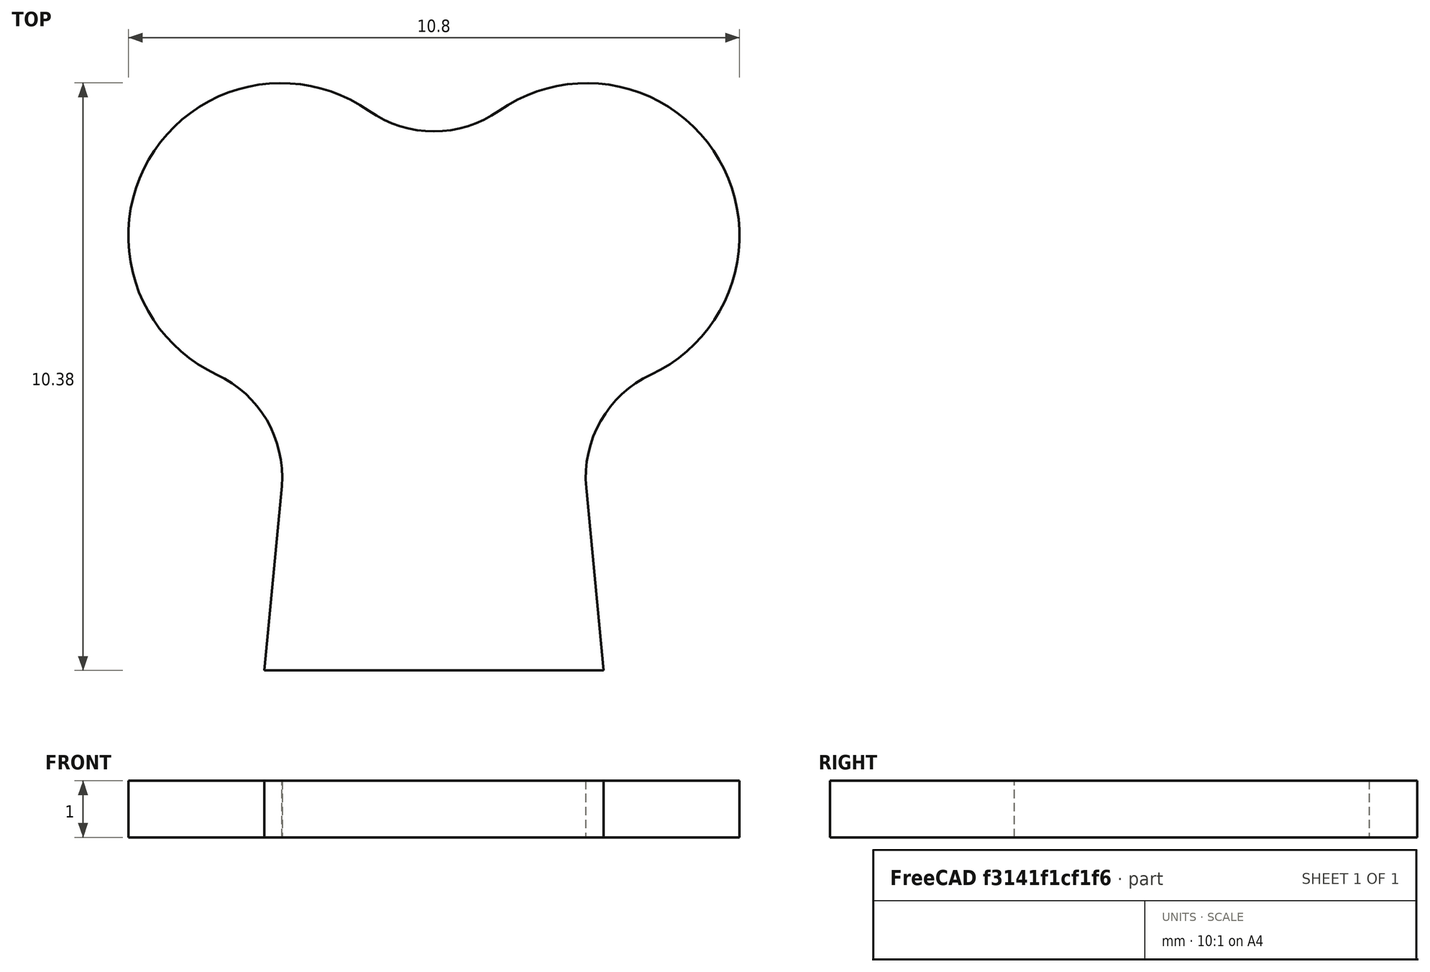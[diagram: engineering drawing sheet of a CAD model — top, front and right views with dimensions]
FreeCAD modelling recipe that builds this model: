
FCSTD DOCUMENT  (FreeCAD 0.18.1R)
Label: PCB_Telemetre_Diametral
License: All rights reserved
LicenseURL: http://en.wikipedia.org/wiki/All_rights_reserved
objects: Sketcher::SketchObject×1, PartDesign::Pad×1, PartDesign::Body×1
note: 4 computed .brp shape members not serialized (recipe doc carries the construction recipe); baked Part::Feature solids carry a one-line shape summary decoded from their .brp

FEATURE [Sketcher::SketchObject] Sketch
  MapMode = 5
  Support = -> [XY_Plane]
  sketch-geometry (11):
    g0: LineSegment StartX=3 StartY=0 StartZ=0 EndX=-3 EndY=0 EndZ=0
    g1: Circle [constr] CenterX=-2.7 CenterY=7.67654 CenterZ=0 NormalX=0 NormalY=0 NormalZ=1 AngleXU=0 Radius=2.7
    g2: Circle [constr] CenterX=2.7 CenterY=7.67654 CenterZ=0 NormalX=0 NormalY=0 NormalZ=1 AngleXU=0 Radius=2.7
    g3: Circle [constr] CenterX=0 CenterY=3 CenterZ=0 NormalX=0 NormalY=0 NormalZ=1 AngleXU=0 Radius=2.7
    g4: ArcOfCircle CenterX=0 CenterY=11.5236 CenterZ=0 NormalX=0 NormalY=0 NormalZ=1 AngleXU=0 Radius=2 StartAngle=4.10043 EndAngle=5.32434
    g5: ArcOfCircle CenterX=-2.7 CenterY=7.67654 CenterZ=0 NormalX=0 NormalY=0 NormalZ=1 AngleXU=0 Radius=2.7 StartAngle=0.958846 EndAngle=4.27718
    g6: ArcOfCircle CenterX=-4.68151 CenterY=3.41466 CenterZ=0 NormalX=0 NormalY=0 NormalZ=1 AngleXU=0 Radius=2 StartAngle=6.20461 EndAngle=7.41878
    g7: LineSegment StartX=-3 StartY=0 StartZ=0 EndX=-2.68768 EndY=3.25767 EndZ=0
    g8: ArcOfCircle CenterX=2.7 CenterY=7.67654 CenterZ=0 NormalX=0 NormalY=0 NormalZ=1 AngleXU=0 Radius=2.7 StartAngle=5.14766 EndAngle=8.46594
    g9: ArcOfCircle CenterX=4.68178 CenterY=3.41479 CenterZ=0 NormalX=0 NormalY=0 NormalZ=1 AngleXU=0 Radius=2 StartAngle=2.00607 EndAngle=3.23717
    g10: LineSegment StartX=3 StartY=0 StartZ=0 EndX=2.69091 EndY=3.22391 EndZ=0
  constraints (31):
    c: PointOnObject(g0,g-1)
    c: Radius(g3) = 2.7
    c: Equal(g3,g2)
    c: Distance(g3,g0) = 3
    c: Tangent(g1,g3)
    c: Tangent(g2,g1)
    c: Tangent(g2,g3)
    c: Symmetric(g1,g2,g-2)
    c: PointOnObject(g4,g2)
    c: PointOnObject(g4,g1)
    c: PointOnObject(g4,g-2)
    c: PointOnObject(g3,g-2)
    c: Tangent(g4,g2)
    c: Coincident(g5,g1)
    c: Coincident(g5,g4)
    c: PointOnObject(g6,g3)
    c: Coincident(g7,g0)
    c: Tangent(g6,g5) = 1.5708
    c: DistanceX(g0,g0) = 6
    c: Symmetric(g0,g0,g-2)
    c: Coincident(g8,g2)
    c: Coincident(g8,g4)
    c: Coincident(g10,g0)
    c: Tangent(g9,g8) = 1.5708
    c: Tangent(g10,g9) = 1.5708
    c: Tangent(g10,g3)
    c: Tangent(g7,g3)
    c: Radius(g9) = 2
    c: Equal(g9,g6)
    c: Equal(g9,g4)
    c: Coincident(g6,g7)
FEATURE [PartDesign::Pad] Pad
  Length = 1
  Length2 = 100
  Profile = -> Sketch
  Type = 0
FEATURE [PartDesign::Body] Body
  Group = -> [Sketch,Pad]
  Origin = -> Origin
  Tip = -> Pad
